# Revit family: Hager-GOLF-Surface_mounted-IP40-With_Cover-With_DIN-NoHosted-CH-fr
name_source: partatom
category: Electrical Equipment
units: mm (PartAtom-declared; Revit-internal decimal feet)

## family parameters
Always vertical = Yes
Cut with Voids When Loaded = No
Maintain Annotation Orientation = No
Panel Configuration = Two Columns, Circuits Across
Part Type = Panelboard
Room Calculation Point = No
Round Connector Dimension = Use Diameter
Shared = No
Work Plane-Based = Yes

## types (18) — shared parameters
Code hager = ADD-EC000214_EU
Default Elevation = 1200 mm
EF000003 - mode de montage = apparent
EF000007 - couleur = blanc
EF000024 - résiste aux UV = No
EF000049 - profondeur = 99 mm  [stored 0.324803 ft]
EF000116 - numéro RAL = 9010
EF000118 - avec plaque de montage = No
EF001062 - version CEM = No
EF001088 - possibilité de montage adossé = Yes
EF001134 - rail DIN = Yes
EF004462 - type de fermeture = autre
EF005474 - indice de protection (IP) = IP40
EF006306 - avec serrure = No
EF009212 - type de couvercle = fermé
EF015941 - porte de transmission du signal = Yes
ETIM class code = EC000214
ETIM class name = Small distribution board
HG000001-nombre de colonnes = 1
HG000002-avec porte = Yes
HG000003-Gamme = GOLF
HG000005-Epaisseur = 2 mm  [stored 0.00656168 ft]
HG000006-Encastré = No
HG000009-Porte à double battant = No
HG000010-Portes asymétriques = No
HG000011-Rangées du bas vides = No
HG000012-Angle de pivotement de la porte = 90.00°
HG000013-Porte à gauche = No
HG000014-Porte à droite = Yes
HG000015-Visibilité de l'emprise de la porte = Yes
HG000016-Visibilité de la porte 3D = Yes
HG000017-Distance entre pôles = 18 mm  [stored 0.0590551 ft]
HG000060-RAL-number = 9010
HG000099-ID modèle Onfly = 507532
Manufacturer = Hager
Name BIM&CO = Electricity
Name hager = ADD_Enclosures_EC000214
Reference = Template-Enclosure_EU-EC000214
Uniformat = Low Tension Service & Dist.
Uniformat code = D501001
zero-valued in all types: EF000218 - profondeur de montage, EF000332 - hauteur d'installation, EF000846 - largeur d'encastrement, EF001131 - profondeur interne, HG000007-Nombre de colonnes vides, HG000008-Nombre de rangées vides

## per-type parameters (varying)
| type | BC_METADATA | EF000008 - largeur | EF000040 - hauteur | EF000266 - nombre de rangées | EF002950 - nombre d'unités modulaires | EF006244 - couvercle/porte transparente | EF015776 - borne de mise à la terre | EF015777 - borne à conducteur neutre | HG000004-Référence fabricant | HGEF000266-Nombre de rangées | HGEF0002950-largeur en nombre de modules |
| GOLF-Surface_mounted_W138_H184_D99_4_Modular_Spacing-VS104PS | {"ObjectGuid":"8e5c2f8d-6d0b-4beb-afcd-b7658456ab24","ModelGuid":"6d0d1f94-98f4-4366-94e4-6df4ac995f1b","VariantGuid":"ee4d26b2-7b4f-49a2-8e25-650d9bad93af","Revision":"#30","VariantName":"GOLF-Surface_mounted_W138_H184_D99_4_Modular_Spacing-VS104PS"} | 138 mm  [stored 0.452756 ft] | 184 mm  [stored 0.603675 ft] | 1 | 4 | No | No | No | VS104PS | 1 | 4 |
| GOLF-Surface_mounted_W138_H184_D99_4_Modular_Spacing-VS104TS | {"ObjectGuid":"8e5c2f8d-6d0b-4beb-afcd-b7658456ab24","ModelGuid":"6d0d1f94-98f4-4366-94e4-6df4ac995f1b","VariantGuid":"293ceb73-ea61-41a1-ba3f-d066f4d82cfd","Revision":"#30","VariantName":"GOLF-Surface_mounted_W138_H184_D99_4_Modular_Spacing-VS104TS"} | 138 mm  [stored 0.452756 ft] | 184 mm  [stored 0.603675 ft] | 1 | 4 | Yes | No | No | VS104TS | 1 | 4 |
| GOLF-Surface_mounted_W210_H184_D99_8_Modular_Spacing-VS108TS | {"ObjectGuid":"8e5c2f8d-6d0b-4beb-afcd-b7658456ab24","ModelGuid":"6d0d1f94-98f4-4366-94e4-6df4ac995f1b","VariantGuid":"aa894ce0-e56e-4b0f-b323-6947d04b306d","Revision":"#30","VariantName":"GOLF-Surface_mounted_W210_H184_D99_8_Modular_Spacing-VS108TS"} | 210 mm  [stored 0.688976 ft] | 184 mm  [stored 0.603675 ft] | 1 | 8 | Yes | No | No | VS108TS | 1 | 8 |
| GOLF-Surface_mounted_W282_H252_D99_12_Modular_Spacing-VS112PS | {"ObjectGuid":"8e5c2f8d-6d0b-4beb-afcd-b7658456ab24","ModelGuid":"6d0d1f94-98f4-4366-94e4-6df4ac995f1b","VariantGuid":"011282b9-2223-4fa8-bf35-43b40c784641","Revision":"#30","VariantName":"GOLF-Surface_mounted_W282_H252_D99_12_Modular_Spacing-VS112PS"} | 282 mm | 252 mm  [stored 0.826772 ft] | 1 | 12 | No | Yes | Yes | VS112PS | 1 | 12 |
| GOLF-Surface_mounted_W282_H252_D99_12_Modular_Spacing-VS112TS | {"ObjectGuid":"8e5c2f8d-6d0b-4beb-afcd-b7658456ab24","ModelGuid":"6d0d1f94-98f4-4366-94e4-6df4ac995f1b","VariantGuid":"26c8d925-6b06-48d2-9fac-9ac562a2837e","Revision":"#30","VariantName":"GOLF-Surface_mounted_W282_H252_D99_12_Modular_Spacing-VS112TS"} | 282 mm | 252 mm  [stored 0.826772 ft] | 1 | 12 | Yes | Yes | Yes | VS112TS | 1 | 12 |
| GOLF-Surface_mounted_W390_H252_D99_18_Modular_Spacing-VS118PS | {"ObjectGuid":"8e5c2f8d-6d0b-4beb-afcd-b7658456ab24","ModelGuid":"6d0d1f94-98f4-4366-94e4-6df4ac995f1b","VariantGuid":"a573df2d-532e-4f90-97ce-38c553c73400","Revision":"#30","VariantName":"GOLF-Surface_mounted_W390_H252_D99_18_Modular_Spacing-VS118PS"} | 390 mm  [stored 1.27953 ft] | 252 mm  [stored 0.826772 ft] | 1 | 18 | No | Yes | Yes | VS118PS | 1 | 18 |
| GOLF-Surface_mounted_W390_H252_D99_18_Modular_Spacing-VS118TS | {"ObjectGuid":"8e5c2f8d-6d0b-4beb-afcd-b7658456ab24","ModelGuid":"6d0d1f94-98f4-4366-94e4-6df4ac995f1b","VariantGuid":"33ebf8c3-556c-462b-9180-3f987eac236c","Revision":"#30","VariantName":"GOLF-Surface_mounted_W390_H252_D99_18_Modular_Spacing-VS118TS"} | 390 mm  [stored 1.27953 ft] | 252 mm  [stored 0.826772 ft] | 1 | 18 | Yes | Yes | Yes | VS118TS | 1 | 18 |
| GOLF-Surface_mounted_W462_H252_D99_22_Modular_Spacing-VS122PS | {"ObjectGuid":"8e5c2f8d-6d0b-4beb-afcd-b7658456ab24","ModelGuid":"6d0d1f94-98f4-4366-94e4-6df4ac995f1b","VariantGuid":"9ca54ec5-dafb-4b75-86a4-5e47a364d618","Revision":"#30","VariantName":"GOLF-Surface_mounted_W462_H252_D99_22_Modular_Spacing-VS122PS"} | 462 mm  [stored 1.51575 ft] | 252 mm  [stored 0.826772 ft] | 1 | 22 | No | Yes | Yes | VS122PS | 1 | 22 |
| GOLF-Surface_mounted_W282_H377_D99_12_Modular_Spacing-VS212PS | {"ObjectGuid":"8e5c2f8d-6d0b-4beb-afcd-b7658456ab24","ModelGuid":"6d0d1f94-98f4-4366-94e4-6df4ac995f1b","VariantGuid":"ce9adaa4-4250-4987-9c77-f54fcbdc8280","Revision":"#30","VariantName":"GOLF-Surface_mounted_W282_H377_D99_12_Modular_Spacing-VS212PS"} | 282 mm | 377 mm  [stored 1.23688 ft] | 2 | 12 | No | Yes | Yes | VS212PS | 2 | 12 |
| GOLF-Surface_mounted_W282_H377_D99_12_Modular_Spacing-VS212TS | {"ObjectGuid":"8e5c2f8d-6d0b-4beb-afcd-b7658456ab24","ModelGuid":"6d0d1f94-98f4-4366-94e4-6df4ac995f1b","VariantGuid":"67df8c00-3a35-4d29-920c-20e84cddecf8","Revision":"#30","VariantName":"GOLF-Surface_mounted_W282_H377_D99_12_Modular_Spacing-VS212TS"} | 282 mm | 377 mm  [stored 1.23688 ft] | 2 | 12 | Yes | Yes | Yes | VS212TS | 2 | 12 |
| GOLF-Surface_mounted_W390_H377_D99_18_Modular_Spacing-VS218PS | {"ObjectGuid":"8e5c2f8d-6d0b-4beb-afcd-b7658456ab24","ModelGuid":"6d0d1f94-98f4-4366-94e4-6df4ac995f1b","VariantGuid":"51c64b5b-224a-4675-a4a7-baabe02800b4","Revision":"#30","VariantName":"GOLF-Surface_mounted_W390_H377_D99_18_Modular_Spacing-VS218PS"} | 390 mm  [stored 1.27953 ft] | 377 mm  [stored 1.23688 ft] | 2 | 18 | No | Yes | Yes | VS218PS | 2 | 18 |
| GOLF-Surface_mounted_W390_H377_D99_18_Modular_Spacing-VS218TS | {"ObjectGuid":"8e5c2f8d-6d0b-4beb-afcd-b7658456ab24","ModelGuid":"6d0d1f94-98f4-4366-94e4-6df4ac995f1b","VariantGuid":"f55fb60a-1cb1-4094-b54a-ba89c9a2113c","Revision":"#30","VariantName":"GOLF-Surface_mounted_W390_H377_D99_18_Modular_Spacing-VS218TS"} | 390 mm  [stored 1.27953 ft] | 377 mm  [stored 1.23688 ft] | 2 | 18 | Yes | Yes | Yes | VS218TS | 2 | 18 |
| GOLF-Surface_mounted_W282_H500_D99_12_Modular_Spacing-VS312PS | {"ObjectGuid":"8e5c2f8d-6d0b-4beb-afcd-b7658456ab24","ModelGuid":"6d0d1f94-98f4-4366-94e4-6df4ac995f1b","VariantGuid":"0b44ae69-8f7f-4ece-9c38-760063e7fc56","Revision":"#30","VariantName":"GOLF-Surface_mounted_W282_H500_D99_12_Modular_Spacing-VS312PS"} | 282 mm | 500 mm  [stored 1.64042 ft] | 3 | 12 | No | Yes | Yes | VS312PS | 3 | 12 |
| GOLF-Surface_mounted_W390_H500_D99_18_Modular_Spacing-VS318PS | {"ObjectGuid":"8e5c2f8d-6d0b-4beb-afcd-b7658456ab24","ModelGuid":"6d0d1f94-98f4-4366-94e4-6df4ac995f1b","VariantGuid":"8c0c5843-ff89-486a-bbdf-574a4de1e79b","Revision":"#30","VariantName":"GOLF-Surface_mounted_W390_H500_D99_18_Modular_Spacing-VS318PS"} | 390 mm  [stored 1.27953 ft] | 500 mm  [stored 1.64042 ft] | 3 | 18 | No | Yes | Yes | VS318PS | 3 | 18 |
| GOLF-Surface_mounted_W390_H500_D99_18_Modular_Spacing-VS318TS | {"ObjectGuid":"8e5c2f8d-6d0b-4beb-afcd-b7658456ab24","ModelGuid":"6d0d1f94-98f4-4366-94e4-6df4ac995f1b","VariantGuid":"db91748b-8776-44cd-9e48-85332eb91ccc","Revision":"#30","VariantName":"GOLF-Surface_mounted_W390_H500_D99_18_Modular_Spacing-VS318TS"} | 390 mm  [stored 1.27953 ft] | 500 mm  [stored 1.64042 ft] | 3 | 18 | Yes | Yes | Yes | VS318TS | 3 | 18 |
| GOLF-Surface_mounted_W282_H647_D99_12_Modular_Spacing-VS412PS | {"ObjectGuid":"8e5c2f8d-6d0b-4beb-afcd-b7658456ab24","ModelGuid":"6d0d1f94-98f4-4366-94e4-6df4ac995f1b","VariantGuid":"7674eb71-3e0c-4b5f-bf94-cf5a896bec66","Revision":"#30","VariantName":"GOLF-Surface_mounted_W282_H647_D99_12_Modular_Spacing-VS412PS"} | 282 mm | 647 mm  [stored 2.1227 ft] | 4 | 12 | No | Yes | Yes | VS412PS | 4 | 12 |
| GOLF-Surface_mounted_W390_H647_D99_18_Modular_Spacing-VS418PS | {"ObjectGuid":"8e5c2f8d-6d0b-4beb-afcd-b7658456ab24","ModelGuid":"6d0d1f94-98f4-4366-94e4-6df4ac995f1b","VariantGuid":"02b4ecfd-22a4-4b2d-b2b1-ca426c26ef76","Revision":"#30","VariantName":"GOLF-Surface_mounted_W390_H647_D99_18_Modular_Spacing-VS418PS"} | 390 mm  [stored 1.27953 ft] | 647 mm  [stored 2.1227 ft] | 4 | 18 | No | Yes | Yes | VS418PS | 4 | 18 |
| GOLF-Surface_mounted_W390_H647_D99_18_Modular_Spacing-VS418TS | {"ObjectGuid":"8e5c2f8d-6d0b-4beb-afcd-b7658456ab24","ModelGuid":"6d0d1f94-98f4-4366-94e4-6df4ac995f1b","VariantGuid":"8b20f88d-4b8d-4d6d-bace-ed5706c15757","Revision":"#30","VariantName":"GOLF-Surface_mounted_W390_H647_D99_18_Modular_Spacing-VS418TS"} | 390 mm  [stored 1.27953 ft] | 647 mm  [stored 2.1227 ft] | 4 | 18 | Yes | Yes | Yes | VS418TS | 4 | 18 |

note: [stored X ft] marks values corroborated as IEEE doubles in the binary element streams (Revit-internal decimal feet)

## geometry (parser evidence)
native form markers: Sweep x17
no freeform markers — native parametric forms only
